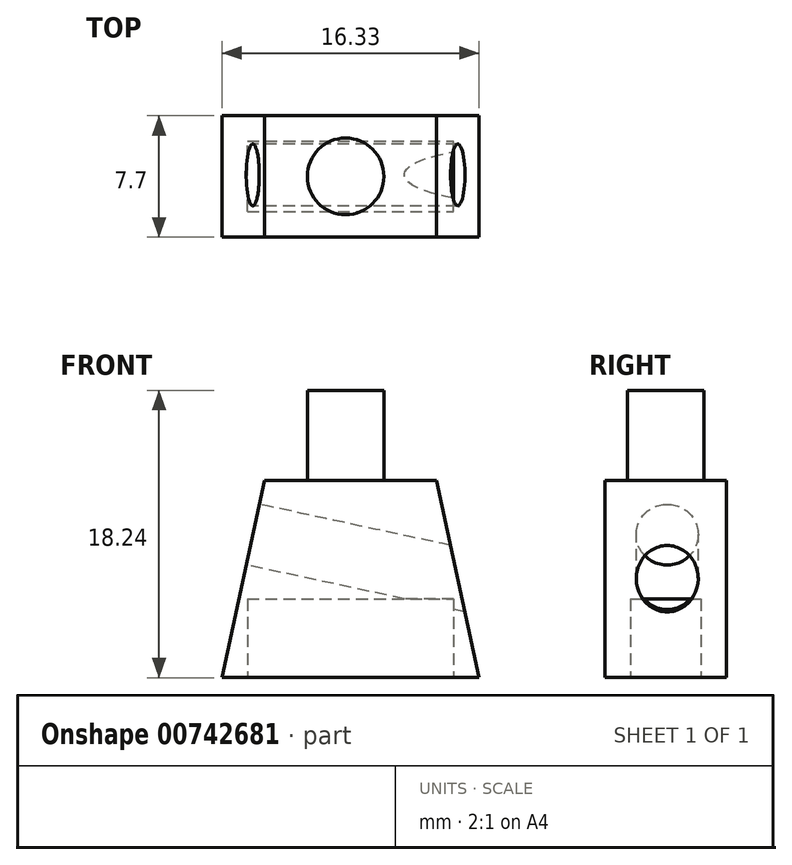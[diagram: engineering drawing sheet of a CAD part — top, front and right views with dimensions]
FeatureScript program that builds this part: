
annotation { "Feature Type Name" : "Feature", "Feature Type Description" : "" }
export const myFeature = defineFeature(function(context is Context, id is Id, definition is map)
    precondition{}
    {
        {
            var Q0;
            Q0=qCreatedBy(makeId("Front.planeOp"),FACE);
            var sketch = newSketch(context, id + "F0", { "sketchPlane" : qUnion([Q0])});
            skLineSegment(sketch, "E0", {"start": v(-41.23, 48.09) * mm, "end": v(-43.93, 35.55) * mm});
            skLineSegment(sketch, "E1", {"start": v(-43.93, 35.55) * mm, "end": v(-27.6, 35.55) * mm});
            skLineSegment(sketch, "E2", {"start": v(-27.6, 35.55) * mm, "end": v(-30.3, 48.09) * mm});
            skLineSegment(sketch, "E3", {"start": v(-30.3, 48.09) * mm, "end": v(-41.23, 48.09) * mm});
            skSolve(sketch);
        }
        {
            var Q0;
            Q0 = qSketchRegion(id + "F0", true);
            extrude(context, id + "F1", {"entities" : qUnion([Q0]), "depth" : 7.7 * mm, "offsetDistance" : 25 * mm});
        }
        {
            var Q0;
            Q0=makeQuery(id+"F1.opExtrude","SWEPT_FACE",FACE,{"disambiguationData":[OSD([sQuery(id+"F0.wireOp",EDGE,"E0")])]});
            var sketch = newSketch(context, id + "F2", { "sketchPlane" : qUnion([Q0])});
            skCircle(sketch, "E4", {"center": v(3.75, 34.82) * mm, "radius": 1.97 * mm});
            skPoint(sketch, "E5.start.orphan", {"position": v(7.7, 34.82) * mm});
            skSolve(sketch);
        }
        {
            var Q0;
            Q0 = qSketchRegion(id + "F2", true);
            extrude(context, id + "F3", {"entities" : qUnion([Q0]), "operationType" : NewBodyOperationType.REMOVE, "oppositeDirection" : true, "depth" : 25 * mm, "offsetDistance" : 25 * mm});
        }
        {
            var Q0;
            Q0=makeQuery(id+"F1.opExtrude","SWEPT_FACE",FACE,{"disambiguationData":[OSD([sQuery(id+"F0.wireOp",EDGE,"E3")])]});
            var sketch = newSketch(context, id + "F4", { "sketchPlane" : qUnion([Q0])});
            skCircle(sketch, "E6", {"center": v(-36.08, -3.85) * mm, "radius": 2.43 * mm});
            skPoint(sketch, "E7.start.orphan", {"position": v(-36.08, -1.41) * mm});
            skPoint(sketch, "E8.start.orphan", {"position": v(-33.64, -3.85) * mm});
            skPoint(sketch, "E9.start.orphan", {"position": v(-36.08, -6.29) * mm});
            skPoint(sketch, "E10.start.orphan", {"position": v(-38.51, -3.85) * mm});
            skSolve(sketch);
        }
        {
            var Q0;
            Q0 = qSketchRegion(id + "F4", true);
            extrude(context, id + "F5", {"entities" : qUnion([Q0]), "operationType" : NewBodyOperationType.ADD, "depth" : 5.7 * mm, "offsetDistance" : 25 * mm});
        }
        {
            var Q0;
            Q0=makeQuery(id+"F1.opExtrude","SWEPT_FACE",FACE,{"disambiguationData":[OSD([sQuery(id+"F0.wireOp",EDGE,"E1")])]});
            var sketch = newSketch(context, id + "F6", { "sketchPlane" : qUnion([Q0])});
            skLineSegment(sketch, "E11.bottom", {"start": v(-42.32, 6.1) * mm, "end": v(-29.2, 6.1) * mm});
            skLineSegment(sketch, "E11.top", {"start": v(-42.32, 1.61) * mm, "end": v(-29.2, 1.61) * mm});
            skLineSegment(sketch, "E11.left", {"start": v(-42.32, 6.09) * mm, "end": v(-42.32, 1.6) * mm});
            skLineSegment(sketch, "E11.right", {"start": v(-29.2, 6.09) * mm, "end": v(-29.2, 1.6) * mm});
            skPoint(sketch, "E12.end.orphan", {"position": v(-38.46, 6.1) * mm});
            skPoint(sketch, "E13.start.orphan", {"position": v(-29.2, 3.85) * mm});
            skPoint(sketch, "E14.start.orphan", {"position": v(-43.93, 3.85) * mm});
            skPoint(sketch, "E15.end.orphan", {"position": v(-35.76, 0) * mm});
            skPoint(sketch, "E15.start.orphan", {"position": v(-35.76, 1.61) * mm});
            skLineSegment(sketch, "E16", {"start": v(-37.9, 1.61) * mm, "end": v(-37.53, 2.13) * mm});
            skLineSegment(sketch, "E17", {"start": v(-37.53, 2.13) * mm, "end": v(-37.18, 2.13) * mm});
            skLineSegment(sketch, "E18", {"start": v(-37.18, 2.13) * mm, "end": v(-37.18, 1.61) * mm});
            skLineSegment(sketch, "E19", {"start": v(-33.38, 1.61) * mm, "end": v(-33.78, 2.13) * mm});
            skLineSegment(sketch, "E20", {"start": v(-33.78, 2.13) * mm, "end": v(-34.18, 2.13) * mm});
            skLineSegment(sketch, "E21", {"start": v(-34.18, 2.13) * mm, "end": v(-34.18, 1.61) * mm});
            skLineSegment(sketch, "E22", {"start": v(-37.9, 6.1) * mm, "end": v(-37.53, 5.58) * mm});
            skLineSegment(sketch, "E23", {"start": v(-37.53, 5.58) * mm, "end": v(-37.18, 5.58) * mm});
            skLineSegment(sketch, "E24", {"start": v(-37.18, 5.58) * mm, "end": v(-37.18, 6.1) * mm});
            skLineSegment(sketch, "E25", {"start": v(-34.18, 6.1) * mm, "end": v(-34.18, 5.58) * mm});
            skLineSegment(sketch, "E26", {"start": v(-34.18, 5.58) * mm, "end": v(-33.78, 5.58) * mm});
            skLineSegment(sketch, "E27", {"start": v(-33.78, 5.58) * mm, "end": v(-33.38, 6.1) * mm});
            skLineSegment(sketch, "E28", {"start": v(-37.9, 6.1) * mm, "end": v(-37.18, 6.1) * mm});
            skLineSegment(sketch, "E29", {"start": v(-34.18, 6.1) * mm, "end": v(-33.38, 6.1) * mm});
            skLineSegment(sketch, "E30", {"start": v(-37.9, 1.61) * mm, "end": v(-37.18, 1.61) * mm});
            skLineSegment(sketch, "E31", {"start": v(-34.18, 1.61) * mm, "end": v(-33.38, 1.61) * mm});
            skSolve(sketch);
        }
        {
            var Q0;
            Q0=makeQuery(id+"F6.imprint","IMPRINT",FACE,{"disambiguationData":[TD([[makeQuery(id+"F6.imprint","IMPRINT",EDGE,{"derivedFrom":sQuery(id+"F6.wireOp",EDGE,"E16")}),-1.0]])]});
            var Q1;
            Q1=makeQuery(id+"F6.imprint","IMPRINT",FACE,{"disambiguationData":[TD([[makeQuery(id+"F6.imprint","IMPRINT",EDGE,{"derivedFrom":sQuery(id+"F6.wireOp",EDGE,"E19")}),1.0]])]});
            var Q2;
            Q2=makeQuery(id+"F6.imprint","IMPRINT",FACE,{"disambiguationData":[TD([[makeQuery(id+"F6.imprint","IMPRINT",EDGE,{"derivedFrom":sQuery(id+"F6.wireOp",EDGE,"E22")}),1.0]])]});
            var Q3;
            Q3=makeQuery(id+"F6.imprint","IMPRINT",FACE,{"disambiguationData":[TD([[makeQuery(id+"F6.imprint","IMPRINT",EDGE,{"derivedFrom":sQuery(id+"F6.wireOp",EDGE,"E25")}),1.0]])]});
            var Q4;
            {var subQ2=sQuery(id+"F6.wireOp",EDGE,"E11.left");Q4=makeQuery(id+"F6.imprint","IMPRINT",FACE,{"disambiguationData":[TD([[makeQuery(id+"F6.imprint","IMPRINT",EDGE,{"derivedFrom":subQ2}),1.0]])]});}
            extrude(context, id + "F7", {"entities" : qUnion([Q0, Q1, Q2, Q3, Q4]), "operationType" : NewBodyOperationType.REMOVE, "oppositeDirection" : true, "depth" : 5 * mm, "offsetDistance" : 25 * mm});
        }
    });
